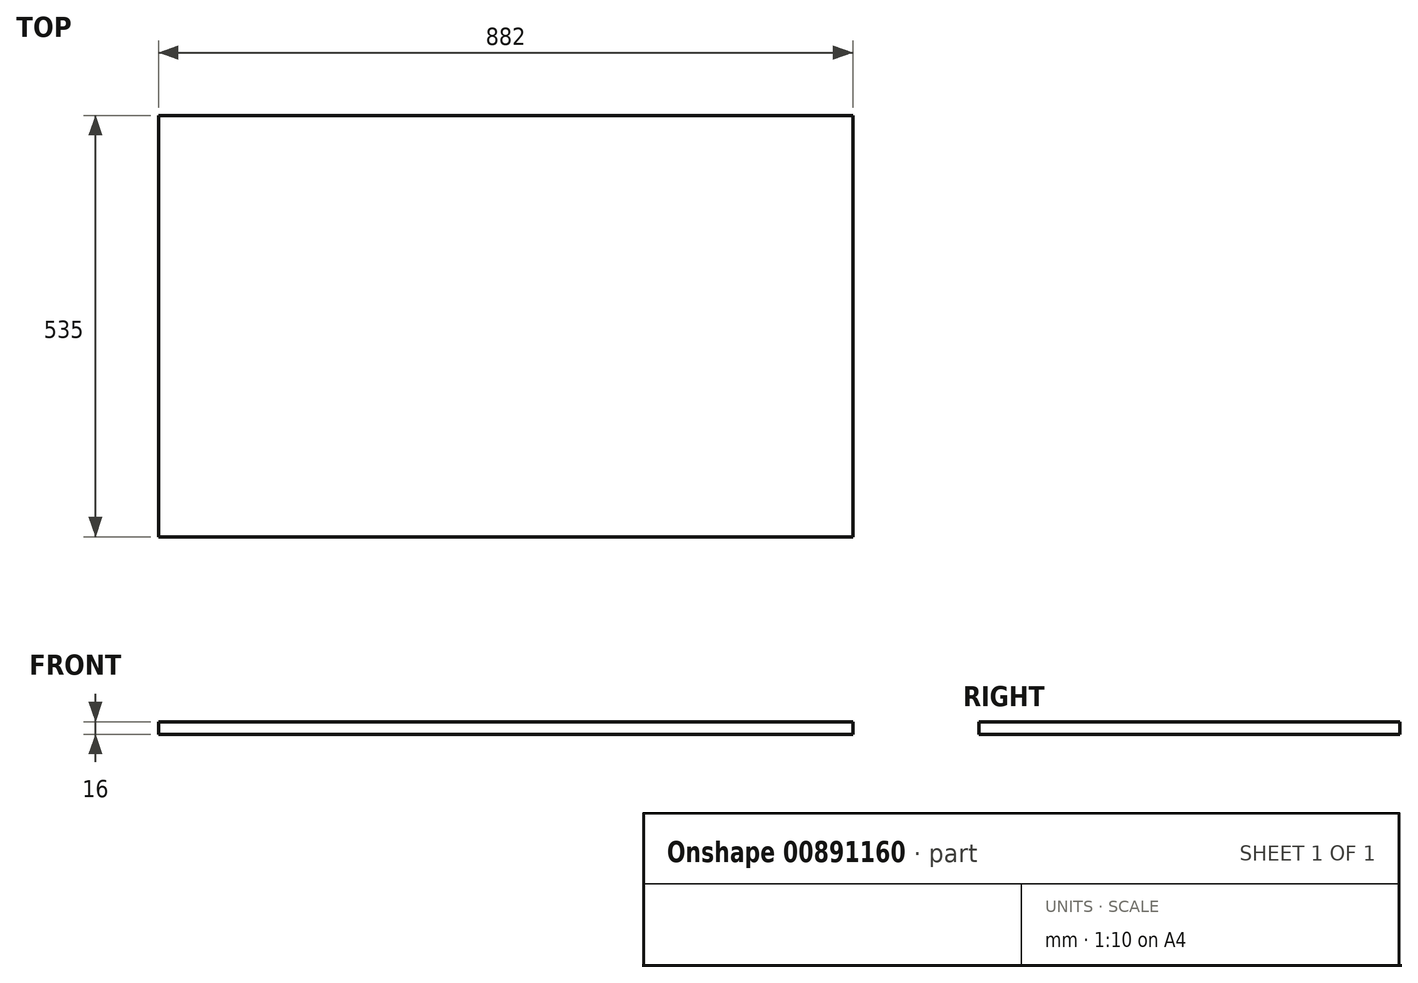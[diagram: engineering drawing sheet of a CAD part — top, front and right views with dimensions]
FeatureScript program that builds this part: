
annotation { "Feature Type Name" : "Feature", "Feature Type Description" : "" }
export const myFeature = defineFeature(function(context is Context, id is Id, definition is map)
    precondition{}
    {
        {
            var Q0;
            Q0=qCreatedBy(makeId("Top.planeOp"),FACE);
            var sketch = newSketch(context, id + "F0", { "sketchPlane" : qUnion([Q0])});
            skLineSegment(sketch, "E0.bottom", {"start": v(-423.53, 283.87) * mm, "end": v(458.47, 283.87) * mm});
            skLineSegment(sketch, "E0.top", {"start": v(-423.53, -251.13) * mm, "end": v(458.47, -251.13) * mm});
            skLineSegment(sketch, "E0.left", {"start": v(-423.53, 283.87) * mm, "end": v(-423.53, -251.13) * mm});
            skLineSegment(sketch, "E0.right", {"start": v(458.47, 283.87) * mm, "end": v(458.47, -251.13) * mm});
            skSolve(sketch);
        }
        {
            var Q0;
            Q0=makeQuery(id+"F0.imprint","IMPRINT",FACE,{"disambiguationData":[TD([[makeQuery(id+"F0.imprint","IMPRINT",EDGE,{"derivedFrom":sQuery(id+"F0.wireOp",EDGE,"E0.bottom")}),-1.0]])]});
            extrude(context, id + "F1", {"entities" : qUnion([Q0]), "depth" : 16 * mm, "offsetDistance" : 25 * mm});
        }
    });
